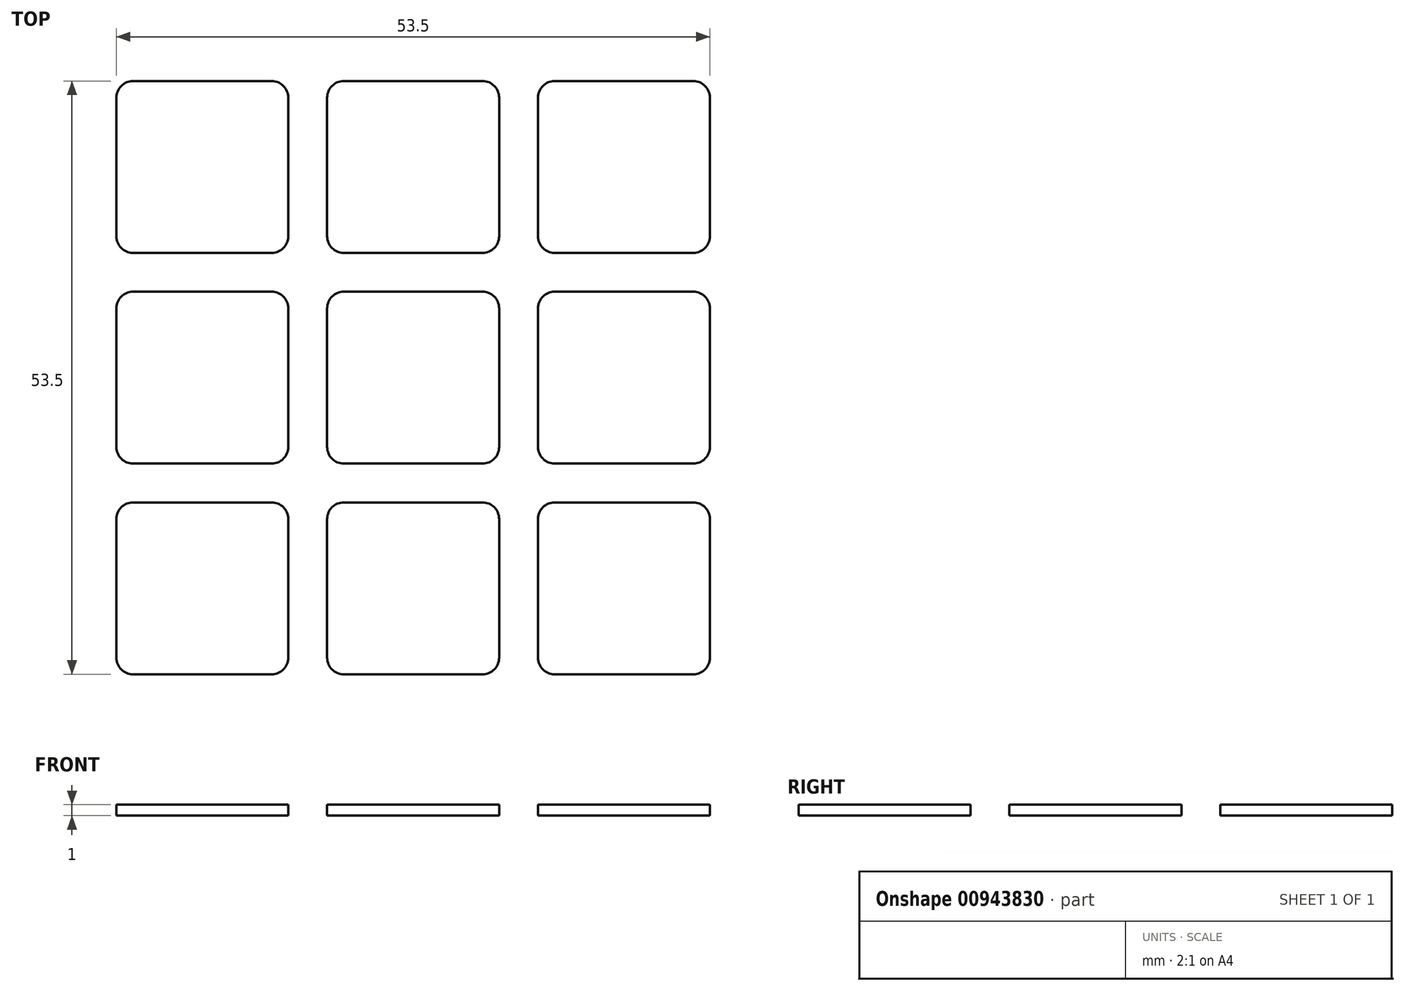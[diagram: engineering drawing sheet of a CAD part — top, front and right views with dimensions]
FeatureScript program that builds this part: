
annotation { "Feature Type Name" : "Feature", "Feature Type Description" : "" }
export const myFeature = defineFeature(function(context is Context, id is Id, definition is map)
    precondition{}
    {
        {
            var Q0;
            Q0=qCreatedBy(makeId("Top.planeOp"),FACE);
            var sketch = newSketch(context, id + "F0", { "sketchPlane" : qUnion([Q0])});
            skLineSegment(sketch, "E0.bottom", {"start": v(28.5, 28.5) * mm, "end": v(-28.5, 28.5) * mm, "construction": true});
            skLineSegment(sketch, "E0.top", {"start": v(28.5, -28.5) * mm, "end": v(-28.5, -28.5) * mm, "construction": true});
            skLineSegment(sketch, "E0.left", {"start": v(28.5, 28.5) * mm, "end": v(28.5, -28.5) * mm, "construction": true});
            skLineSegment(sketch, "E0.right", {"start": v(-28.5, 28.5) * mm, "end": v(-28.5, -28.5) * mm, "construction": true});
            skPoint(sketch, "E0.middle", {"position": v(0, 0) * mm});
            skLineSegment(sketch, "E1", {"start": v(-9.5, 28.5) * mm, "end": v(-9.5, -28.5) * mm, "construction": true});
            skLineSegment(sketch, "E2.1.0", {"start": v(-28.5, -9.5) * mm, "end": v(28.5, -9.5) * mm, "construction": true});
            skLineSegment(sketch, "E2.2.0", {"start": v(9.5, -28.5) * mm, "end": v(9.5, 28.5) * mm, "construction": true});
            skLineSegment(sketch, "E2.3.0", {"start": v(28.5, 9.5) * mm, "end": v(-28.5, 9.5) * mm, "construction": true});
            skLineSegment(sketch, "E3.bottom", {"start": v(-25.25, -11.25) * mm, "end": v(-12.75, -11.25) * mm});
            skLineSegment(sketch, "E3.top", {"start": v(-25.25, -26.75) * mm, "end": v(-12.75, -26.75) * mm});
            skLineSegment(sketch, "E3.left", {"start": v(-26.75, -12.75) * mm, "end": v(-26.75, -25.25) * mm});
            skLineSegment(sketch, "E3.right", {"start": v(-11.25, -12.75) * mm, "end": v(-11.25, -25.25) * mm});
            skLineSegment(sketch, "E4.bottom", {"start": v(-6.25, -11.25) * mm, "end": v(6.25, -11.25) * mm});
            skLineSegment(sketch, "E4.top", {"start": v(-6.25, -26.75) * mm, "end": v(6.25, -26.75) * mm});
            skLineSegment(sketch, "E4.left", {"start": v(-7.75, -12.75) * mm, "end": v(-7.75, -25.25) * mm});
            skLineSegment(sketch, "E4.right", {"start": v(7.75, -12.75) * mm, "end": v(7.75, -25.25) * mm});
            skLineSegment(sketch, "E5.bottom", {"start": v(-6.25, 7.75) * mm, "end": v(6.25, 7.75) * mm});
            skLineSegment(sketch, "E5.top", {"start": v(-6.25, -7.75) * mm, "end": v(6.25, -7.75) * mm});
            skLineSegment(sketch, "E5.left", {"start": v(-7.75, 6.25) * mm, "end": v(-7.75, -6.25) * mm});
            skLineSegment(sketch, "E5.right", {"start": v(7.75, 6.25) * mm, "end": v(7.75, -6.25) * mm});
            skPoint(sketch, "E6.visualSharp", {"position": v(-26.75, -11.25) * mm});
            skArc(sketch, "E6.filletArc", {"start": v(-25.25, -11.25) * mm, "mid": v(-26.31, -11.69) * mm, "end": v(-26.75, -12.75) * mm});
            skPoint(sketch, "E7.visualSharp", {"position": v(-11.25, -11.25) * mm});
            skArc(sketch, "E7.filletArc", {"start": v(-11.25, -12.75) * mm, "mid": v(-11.69, -11.69) * mm, "end": v(-12.75, -11.25) * mm});
            skPoint(sketch, "E8.visualSharp", {"position": v(-11.25, -26.75) * mm});
            skArc(sketch, "E8.filletArc", {"start": v(-12.75, -26.75) * mm, "mid": v(-11.69, -26.31) * mm, "end": v(-11.25, -25.25) * mm});
            skPoint(sketch, "E9.visualSharp", {"position": v(-26.75, -26.75) * mm});
            skArc(sketch, "E9.filletArc", {"start": v(-26.75, -25.25) * mm, "mid": v(-26.31, -26.31) * mm, "end": v(-25.25, -26.75) * mm});
            skPoint(sketch, "E10.visualSharp", {"position": v(-7.75, -26.75) * mm});
            skArc(sketch, "E10.filletArc", {"start": v(-7.75, -25.25) * mm, "mid": v(-7.31, -26.31) * mm, "end": v(-6.25, -26.75) * mm});
            skPoint(sketch, "E11.visualSharp", {"position": v(7.75, -26.75) * mm});
            skArc(sketch, "E11.filletArc", {"start": v(6.25, -26.75) * mm, "mid": v(7.31, -26.31) * mm, "end": v(7.75, -25.25) * mm});
            skPoint(sketch, "E12.visualSharp", {"position": v(7.75, -11.25) * mm});
            skArc(sketch, "E12.filletArc", {"start": v(7.75, -12.75) * mm, "mid": v(7.31, -11.69) * mm, "end": v(6.25, -11.25) * mm});
            skPoint(sketch, "E13.visualSharp", {"position": v(-7.75, -11.25) * mm});
            skArc(sketch, "E13.filletArc", {"start": v(-6.25, -11.25) * mm, "mid": v(-7.31, -11.69) * mm, "end": v(-7.75, -12.75) * mm});
            skPoint(sketch, "E14.visualSharp", {"position": v(-7.75, -7.75) * mm});
            skArc(sketch, "E14.filletArc", {"start": v(-7.75, -6.25) * mm, "mid": v(-7.31, -7.31) * mm, "end": v(-6.25, -7.75) * mm});
            skPoint(sketch, "E15.visualSharp", {"position": v(7.75, -7.75) * mm});
            skArc(sketch, "E15.filletArc", {"start": v(6.25, -7.75) * mm, "mid": v(7.31, -7.31) * mm, "end": v(7.75, -6.25) * mm});
            skPoint(sketch, "E16.visualSharp", {"position": v(7.75, 7.75) * mm});
            skArc(sketch, "E16.filletArc", {"start": v(7.75, 6.25) * mm, "mid": v(7.31, 7.31) * mm, "end": v(6.25, 7.75) * mm});
            skPoint(sketch, "E17.visualSharp", {"position": v(-7.75, 7.75) * mm});
            skArc(sketch, "E17.filletArc", {"start": v(-6.25, 7.75) * mm, "mid": v(-7.31, 7.31) * mm, "end": v(-7.75, 6.25) * mm});
            skPoint(sketch, "E18.1.0", {"position": v(11.25, -11.25) * mm});
            skPoint(sketch, "E18.1.1", {"position": v(26.75, -7.75) * mm});
            skLineSegment(sketch, "E18.1.2", {"start": v(26.75, -25.25) * mm, "end": v(26.75, -12.75) * mm});
            skLineSegment(sketch, "E18.1.3", {"start": v(11.25, -25.25) * mm, "end": v(11.25, -12.75) * mm});
            skPoint(sketch, "E18.1.4", {"position": v(11.25, -7.75) * mm});
            skPoint(sketch, "E18.1.5", {"position": v(26.75, -11.25) * mm});
            skLineSegment(sketch, "E18.1.6", {"start": v(12.75, 7.75) * mm, "end": v(25.25, 7.75) * mm});
            skPoint(sketch, "E18.1.7", {"position": v(26.75, -26.75) * mm});
            skPoint(sketch, "E18.1.8", {"position": v(11.25, 7.75) * mm});
            skPoint(sketch, "E18.1.9", {"position": v(11.25, -26.75) * mm});
            skLineSegment(sketch, "E18.1.10", {"start": v(11.25, -6.25) * mm, "end": v(11.25, 6.25) * mm});
            skLineSegment(sketch, "E18.1.11", {"start": v(12.75, -11.25) * mm, "end": v(25.25, -11.25) * mm});
            skPoint(sketch, "E18.1.12", {"position": v(26.75, 7.75) * mm});
            skLineSegment(sketch, "E18.1.13", {"start": v(12.75, -26.75) * mm, "end": v(25.25, -26.75) * mm});
            skLineSegment(sketch, "E18.1.14", {"start": v(26.75, -6.25) * mm, "end": v(26.75, 6.25) * mm});
            skLineSegment(sketch, "E18.1.15", {"start": v(12.75, -7.75) * mm, "end": v(25.25, -7.75) * mm});
            skArc(sketch, "E18.1.16", {"start": v(25.25, -7.75) * mm, "mid": v(26.31, -7.31) * mm, "end": v(26.75, -6.25) * mm});
            skArc(sketch, "E18.1.17", {"start": v(12.75, 7.75) * mm, "mid": v(11.69, 7.31) * mm, "end": v(11.25, 6.25) * mm});
            skArc(sketch, "E18.1.18", {"start": v(26.75, 6.25) * mm, "mid": v(26.31, 7.31) * mm, "end": v(25.25, 7.75) * mm});
            skArc(sketch, "E18.1.19", {"start": v(11.25, -6.25) * mm, "mid": v(11.69, -7.31) * mm, "end": v(12.75, -7.75) * mm});
            skArc(sketch, "E18.1.20", {"start": v(26.75, -12.75) * mm, "mid": v(26.31, -11.69) * mm, "end": v(25.25, -11.25) * mm});
            skArc(sketch, "E18.1.21", {"start": v(11.25, -25.25) * mm, "mid": v(11.69, -26.31) * mm, "end": v(12.75, -26.75) * mm});
            skArc(sketch, "E18.1.22", {"start": v(25.25, -26.75) * mm, "mid": v(26.31, -26.31) * mm, "end": v(26.75, -25.25) * mm});
            skArc(sketch, "E18.1.23", {"start": v(12.75, -11.25) * mm, "mid": v(11.69, -11.69) * mm, "end": v(11.25, -12.75) * mm});
            skPoint(sketch, "E18.2.0", {"position": v(11.25, 11.25) * mm});
            skPoint(sketch, "E18.2.1", {"position": v(7.75, 26.75) * mm});
            skLineSegment(sketch, "E18.2.2", {"start": v(25.25, 26.75) * mm, "end": v(12.75, 26.75) * mm});
            skLineSegment(sketch, "E18.2.3", {"start": v(25.25, 11.25) * mm, "end": v(12.75, 11.25) * mm});
            skPoint(sketch, "E18.2.4", {"position": v(7.75, 11.25) * mm});
            skPoint(sketch, "E18.2.5", {"position": v(11.25, 26.75) * mm});
            skLineSegment(sketch, "E18.2.6", {"start": v(-7.75, 12.75) * mm, "end": v(-7.75, 25.25) * mm});
            skPoint(sketch, "E18.2.7", {"position": v(26.75, 26.75) * mm});
            skPoint(sketch, "E18.2.8", {"position": v(-7.75, 11.25) * mm});
            skPoint(sketch, "E18.2.9", {"position": v(26.75, 11.25) * mm});
            skLineSegment(sketch, "E18.2.10", {"start": v(6.25, 11.25) * mm, "end": v(-6.25, 11.25) * mm});
            skLineSegment(sketch, "E18.2.11", {"start": v(11.25, 12.75) * mm, "end": v(11.25, 25.25) * mm});
            skPoint(sketch, "E18.2.12", {"position": v(-7.75, 26.75) * mm});
            skLineSegment(sketch, "E18.2.13", {"start": v(26.75, 12.75) * mm, "end": v(26.75, 25.25) * mm});
            skLineSegment(sketch, "E18.2.14", {"start": v(6.25, 26.75) * mm, "end": v(-6.25, 26.75) * mm});
            skLineSegment(sketch, "E18.2.15", {"start": v(7.75, 12.75) * mm, "end": v(7.75, 25.25) * mm});
            skArc(sketch, "E18.2.16", {"start": v(7.75, 25.25) * mm, "mid": v(7.31, 26.31) * mm, "end": v(6.25, 26.75) * mm});
            skArc(sketch, "E18.2.17", {"start": v(-7.75, 12.75) * mm, "mid": v(-7.31, 11.69) * mm, "end": v(-6.25, 11.25) * mm});
            skArc(sketch, "E18.2.18", {"start": v(-6.25, 26.75) * mm, "mid": v(-7.31, 26.31) * mm, "end": v(-7.75, 25.25) * mm});
            skArc(sketch, "E18.2.19", {"start": v(6.25, 11.25) * mm, "mid": v(7.31, 11.69) * mm, "end": v(7.75, 12.75) * mm});
            skArc(sketch, "E18.2.20", {"start": v(12.75, 26.75) * mm, "mid": v(11.69, 26.31) * mm, "end": v(11.25, 25.25) * mm});
            skArc(sketch, "E18.2.21", {"start": v(25.25, 11.25) * mm, "mid": v(26.31, 11.69) * mm, "end": v(26.75, 12.75) * mm});
            skArc(sketch, "E18.2.22", {"start": v(26.75, 25.25) * mm, "mid": v(26.31, 26.31) * mm, "end": v(25.25, 26.75) * mm});
            skArc(sketch, "E18.2.23", {"start": v(11.25, 12.75) * mm, "mid": v(11.69, 11.69) * mm, "end": v(12.75, 11.25) * mm});
            skPoint(sketch, "E18.3.0", {"position": v(-11.25, 11.25) * mm});
            skPoint(sketch, "E18.3.1", {"position": v(-26.75, 7.75) * mm});
            skLineSegment(sketch, "E18.3.2", {"start": v(-26.75, 25.25) * mm, "end": v(-26.75, 12.75) * mm});
            skLineSegment(sketch, "E18.3.3", {"start": v(-11.25, 25.25) * mm, "end": v(-11.25, 12.75) * mm});
            skPoint(sketch, "E18.3.4", {"position": v(-11.25, 7.75) * mm});
            skPoint(sketch, "E18.3.5", {"position": v(-26.75, 11.25) * mm});
            skLineSegment(sketch, "E18.3.6", {"start": v(-12.75, -7.75) * mm, "end": v(-25.25, -7.75) * mm});
            skPoint(sketch, "E18.3.7", {"position": v(-26.75, 26.75) * mm});
            skPoint(sketch, "E18.3.8", {"position": v(-11.25, -7.75) * mm});
            skPoint(sketch, "E18.3.9", {"position": v(-11.25, 26.75) * mm});
            skLineSegment(sketch, "E18.3.10", {"start": v(-11.25, 6.25) * mm, "end": v(-11.25, -6.25) * mm});
            skLineSegment(sketch, "E18.3.11", {"start": v(-12.75, 11.25) * mm, "end": v(-25.25, 11.25) * mm});
            skPoint(sketch, "E18.3.12", {"position": v(-26.75, -7.75) * mm});
            skLineSegment(sketch, "E18.3.13", {"start": v(-12.75, 26.75) * mm, "end": v(-25.25, 26.75) * mm});
            skLineSegment(sketch, "E18.3.14", {"start": v(-26.75, 6.25) * mm, "end": v(-26.75, -6.25) * mm});
            skLineSegment(sketch, "E18.3.15", {"start": v(-12.75, 7.75) * mm, "end": v(-25.25, 7.75) * mm});
            skArc(sketch, "E18.3.16", {"start": v(-25.25, 7.75) * mm, "mid": v(-26.31, 7.31) * mm, "end": v(-26.75, 6.25) * mm});
            skArc(sketch, "E18.3.17", {"start": v(-12.75, -7.75) * mm, "mid": v(-11.69, -7.31) * mm, "end": v(-11.25, -6.25) * mm});
            skArc(sketch, "E18.3.18", {"start": v(-26.75, -6.25) * mm, "mid": v(-26.31, -7.31) * mm, "end": v(-25.25, -7.75) * mm});
            skArc(sketch, "E18.3.19", {"start": v(-11.25, 6.25) * mm, "mid": v(-11.69, 7.31) * mm, "end": v(-12.75, 7.75) * mm});
            skArc(sketch, "E18.3.20", {"start": v(-26.75, 12.75) * mm, "mid": v(-26.31, 11.69) * mm, "end": v(-25.25, 11.25) * mm});
            skArc(sketch, "E18.3.21", {"start": v(-11.25, 25.25) * mm, "mid": v(-11.69, 26.31) * mm, "end": v(-12.75, 26.75) * mm});
            skArc(sketch, "E18.3.22", {"start": v(-25.25, 26.75) * mm, "mid": v(-26.31, 26.31) * mm, "end": v(-26.75, 25.25) * mm});
            skArc(sketch, "E18.3.23", {"start": v(-12.75, 11.25) * mm, "mid": v(-11.69, 11.69) * mm, "end": v(-11.25, 12.75) * mm});
            skSolve(sketch);
        }
        {
            var Q0;
            Q0 = qSketchRegion(id + "F0", true);
            extrude(context, id + "F1", {"entities" : qUnion([Q0]), "depth" : 1 * mm, "offsetDistance" : 25 * mm});
        }
    });
